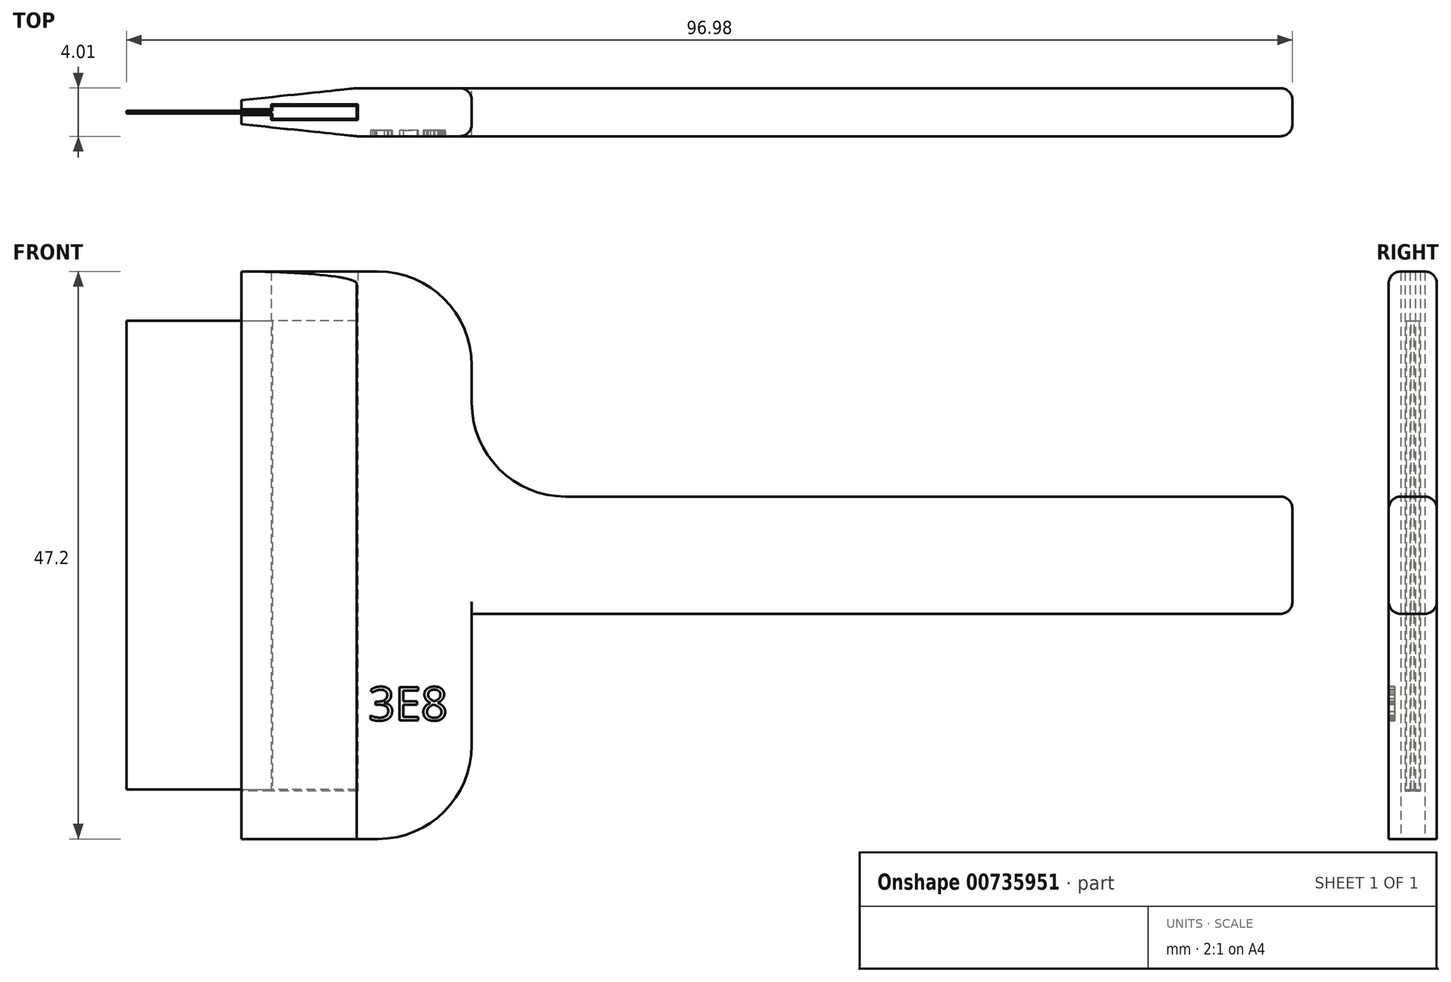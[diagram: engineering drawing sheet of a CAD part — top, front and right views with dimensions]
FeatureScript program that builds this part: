
annotation { "Feature Type Name" : "Feature", "Feature Type Description" : "" }
export const myFeature = defineFeature(function(context is Context, id is Id, definition is map)
    precondition{}
    {
        {
            assignVariable(context, id + "F0", {"name" : "res", "anyValue" : .1});
        }
        {
            assignVariable(context, id + "F1", {"name" : "razorthick", "anyValue" : .25});
        }
        {
            assignVariable(context, id + "F2", {"name" : "razorwidth", "anyValue" : 39});
        }
        {
            assignVariable(context, id + "F3", {"name" : "headthick", "anyValue" : 4});
        }
        {
            var Q0;
            Q0=qCreatedBy(makeId("Front.planeOp"),FACE);
            var sketch = newSketch(context, id + "F4", { "sketchPlane" : qUnion([Q0])});
            skLineSegment(sketch, "E0.bottom", {"start": v(-15.58, 0) * mm, "end": v(3.57, 0) * mm});
            skLineSegment(sketch, "E0.top", {"start": v(-15.58, 39) * mm, "end": v(3.57, 39) * mm});
            skLineSegment(sketch, "E0.left", {"start": v(-15.58, 0) * mm, "end": v(-15.58, 39) * mm});
            skLineSegment(sketch, "E0.right", {"start": v(3.57, 0) * mm, "end": v(3.57, 39) * mm});
            skSolve(sketch);
        }
        {
            var Q0;
            Q0=makeQuery(id+"F4.imprint","IMPRINT",FACE,{"disambiguationData":[TD([[makeQuery(id+"F4.imprint","IMPRINT",EDGE,{"derivedFrom":sQuery(id+"F4.wireOp",EDGE,"E0.bottom")}),1.0]])]});
            extrude(context, id + "F5", {"entities" : qUnion([Q0]), "depth" : (getVariable(context, 'razorthick')) * mm, "offsetDistance" : 25 * mm});
        }
        {
            var Q0;
            Q0=makeQuery(id+"F5.opExtrude","SWEPT_FACE",FACE,{"disambiguationData":[OSD([sQuery(id+"F4.wireOp",EDGE,"E0.bottom")])]});
            var sketch = newSketch(context, id + "F6", { "sketchPlane" : qUnion([Q0])});
            skLineSegment(sketch, "E1.bottom", {"start": v(3.57, 0.67) * mm, "end": v(-3.43, 0.67) * mm});
            skLineSegment(sketch, "E1.top", {"start": v(3.57, -0.41) * mm, "end": v(-3.43, -0.41) * mm});
            skLineSegment(sketch, "E1.left", {"start": v(3.57, 0.66) * mm, "end": v(3.57, -0.41) * mm});
            skLineSegment(sketch, "E1.right", {"start": v(-3.43, 0.66) * mm, "end": v(-3.43, -0.41) * mm});
            skPoint(sketch, "E2", {"position": v(3.57, 0.12) * mm});
            skSolve(sketch);
        }
        {
            var Q0;
            Q0 = qSketchRegion(id + "F6", true);
            var Q1;
            Q1=makeQuery(id+"F5.opExtrude","SWEPT_FACE",FACE,{"disambiguationData":[OSD([sQuery(id+"F4.wireOp",EDGE,"E0.top")])]});
            extrude(context, id + "F7", {"entities" : qUnion([Q0]), "operationType" : NewBodyOperationType.ADD, "endBound" : BoundingType.UP_TO_SURFACE, "oppositeDirection" : true, "depth" : 25 * mm, "endBoundEntityFace" : qUnion([Q1]), "offsetDistance" : 25 * mm});
        }
        {
            var Q0;
            Q0=makeQuery(id+"F7.boolean.opBoolean","MERGE",FACE,{"derivedFrom":[makeQuery(id+"F5.opExtrude","SWEPT_FACE",FACE,{"disambiguationData":[OSD([sQuery(id+"F4.wireOp",EDGE,"E0.bottom")])]}),makeQuery(id+"F7.opExtrude","CAP_FACE",FACE,{"disambiguationData":[OSD([sQuery(id+"F6.wireOp",EDGE,"E1.bottom"),sQuery(id+"F6.wireOp",EDGE,"E1.top"),sQuery(id+"F6.wireOp",EDGE,"E1.left"),sQuery(id+"F6.wireOp",EDGE,"E1.right")])],"isStart":true})]});
            cPlane(context, id + "F8", {"entities" : qUnion([Q0]), "cplaneType" : CPlaneType.OFFSET, "offset" : (getVariable(context, 'res')) * mm, "width" : 150 * mm, "height" : 150 * mm});
        }
        {
            var Q0;
            Q0=qCreatedBy(id+"F8.planeOp",FACE);
            var sketch = newSketch(context, id + "F9", { "sketchPlane" : qUnion([Q0])});
            skLineSegment(sketch, "E3.0.0", {"start": v(3.57, -0.41) * mm, "end": v(3.57, 0.67) * mm, "construction": true});
            skLineSegment(sketch, "E3.0.1", {"start": v(3.57, 0.67) * mm, "end": v(-3.43, 0.67) * mm, "construction": true});
            skLineSegment(sketch, "E3.0.2", {"start": v(-3.43, 0.67) * mm, "end": v(-3.43, 0.25) * mm, "construction": true});
            skLineSegment(sketch, "E3.0.3", {"start": v(-3.43, 0.25) * mm, "end": v(-15.58, 0.25) * mm, "construction": true});
            skLineSegment(sketch, "E3.0.4", {"start": v(-15.58, 0.25) * mm, "end": v(-15.58, 0) * mm, "construction": true});
            skLineSegment(sketch, "E3.0.5", {"start": v(-15.58, 0) * mm, "end": v(-3.43, 0) * mm, "construction": true});
            skLineSegment(sketch, "E3.0.6", {"start": v(-3.43, 0) * mm, "end": v(-3.43, -0.41) * mm, "construction": true});
            skLineSegment(sketch, "E3.0.7", {"start": v(-3.43, -0.41) * mm, "end": v(3.57, -0.41) * mm, "construction": true});
            skLineSegment(sketch, "E4.0", {"start": v(-3.53, -0.51) * mm, "end": v(3.67, -0.51) * mm});
            skLineSegment(sketch, "E4.1", {"start": v(-3.53, -0.1) * mm, "end": v(-3.53, -0.51) * mm});
            skLineSegment(sketch, "E4.2", {"start": v(3.67, -0.51) * mm, "end": v(3.67, 0.76) * mm});
            skLineSegment(sketch, "E4.3", {"start": v(-15.68, -0.1) * mm, "end": v(-3.53, -0.1) * mm});
            skLineSegment(sketch, "E4.4", {"start": v(3.67, 0.76) * mm, "end": v(-3.53, 0.76) * mm});
            skLineSegment(sketch, "E4.5", {"start": v(-3.53, 0.76) * mm, "end": v(-3.53, 0.35) * mm});
            skLineSegment(sketch, "E4.6", {"start": v(-3.53, 0.35) * mm, "end": v(-15.68, 0.35) * mm});
            skLineSegment(sketch, "E4.7", {"start": v(-15.68, 0.35) * mm, "end": v(-15.68, -0.1) * mm});
            skLineSegment(sketch, "E5", {"start": v(3.57, 0.12) * mm, "end": v(-6, 0.12) * mm, "construction": true});
            skLineSegment(sketch, "E6.bottom", {"start": v(-6, -1.88) * mm, "end": v(13.15, -1.88) * mm});
            skLineSegment(sketch, "E6.top", {"start": v(-6, 2.12) * mm, "end": v(13.15, 2.12) * mm});
            skLineSegment(sketch, "E6.left", {"start": v(-6, -1.88) * mm, "end": v(-6, 2.12) * mm});
            skLineSegment(sketch, "E6.right", {"start": v(13.15, -1.88) * mm, "end": v(13.15, 2.12) * mm});
            skPoint(sketch, "E6.middle", {"position": v(3.57, 0.12) * mm});
            skLineSegment(sketch, "E7", {"start": v(-6, 1.12) * mm, "end": v(3.57, 2.12) * mm});
            skLineSegment(sketch, "E8.MirrorCS", {"start": v(-6, -0.87) * mm, "end": v(3.57, -1.87) * mm});
            skSolve(sketch);
        }
        {
            var Q0;
            Q0=makeQuery(id+"F9.imprint","IMPRINT",FACE,{"disambiguationData":[TD([[makeQuery(id+"F9.imprint","IMPRINT",EDGE,{"derivedFrom":sQuery(id+"F9.wireOp",EDGE,"E4.0")}),-1.0]])]});
            extrude(context, id + "F10", {"entities" : qUnion([Q0]), "oppositeDirection" : true, "depth" : (getVariable(context, 'razorwidth') + (2 * getVariable(context, 'res')) + getVariable(context, 'headthick')) * mm, "offsetDistance" : 25 * mm});
        }
        {
            var Q0;
            Q0=makeQuery(id+"F10.opExtrude","CAP_FACE",FACE,{"disambiguationData":[OSD([sQuery(id+"F9.wireOp",EDGE,"E4.0"),sQuery(id+"F9.wireOp",EDGE,"E4.1"),sQuery(id+"F9.wireOp",EDGE,"E4.2"),sQuery(id+"F9.wireOp",EDGE,"E4.3"),sQuery(id+"F9.wireOp",EDGE,"E4.4"),sQuery(id+"F9.wireOp",EDGE,"E4.5"),sQuery(id+"F9.wireOp",EDGE,"E4.6"),sQuery(id+"F9.wireOp",EDGE,"E6.bottom"),sQuery(id+"F9.wireOp",EDGE,"E6.top"),sQuery(id+"F9.wireOp",EDGE,"E6.left"),sQuery(id+"F9.wireOp",EDGE,"E6.right"),sQuery(id+"F9.wireOp",EDGE,"E7"),sQuery(id+"F9.wireOp",EDGE,"E8.MirrorCS")])],"isStart":true});
            var sketch = newSketch(context, id + "F11", { "sketchPlane" : qUnion([Q0])});
            skLineSegment(sketch, "E9.0.0", {"start": v(-6, -0.1) * mm, "end": v(-6, -0.87) * mm});
            skLineSegment(sketch, "E9.0.1", {"start": v(-6, -0.87) * mm, "end": v(3.57, -1.88) * mm});
            skLineSegment(sketch, "E9.0.2", {"start": v(3.57, -1.88) * mm, "end": v(13.15, -1.88) * mm});
            skLineSegment(sketch, "E9.0.3", {"start": v(13.15, -1.88) * mm, "end": v(13.15, 2.12) * mm});
            skLineSegment(sketch, "E9.0.4", {"start": v(13.15, 2.12) * mm, "end": v(3.57, 2.12) * mm});
            skLineSegment(sketch, "E9.0.5", {"start": v(3.57, 2.12) * mm, "end": v(-6, 1.12) * mm});
            skLineSegment(sketch, "E9.0.6", {"start": v(-6, 1.12) * mm, "end": v(-6, 0.35) * mm});
            skLineSegment(sketch, "E9.0.7", {"start": v(-6, 0.35) * mm, "end": v(-3.53, 0.35) * mm, "construction": true});
            skLineSegment(sketch, "E9.0.8", {"start": v(-3.53, 0.35) * mm, "end": v(-3.53, 0.76) * mm, "construction": true});
            skLineSegment(sketch, "E9.0.9", {"start": v(-3.53, 0.76) * mm, "end": v(3.67, 0.76) * mm, "construction": true});
            skLineSegment(sketch, "E9.0.10", {"start": v(3.67, 0.76) * mm, "end": v(3.67, -0.51) * mm, "construction": true});
            skLineSegment(sketch, "E9.0.11", {"start": v(3.67, -0.51) * mm, "end": v(-3.53, -0.51) * mm, "construction": true});
            skLineSegment(sketch, "E9.0.12", {"start": v(-3.53, -0.51) * mm, "end": v(-3.53, -0.1) * mm, "construction": true});
            skLineSegment(sketch, "E9.0.13", {"start": v(-3.53, -0.1) * mm, "end": v(-6, -0.1) * mm, "construction": true});
            skLineSegment(sketch, "E10", {"start": v(-6, -0.1) * mm, "end": v(-6, 0.35) * mm});
            skSolve(sketch);
        }
        {
            var Q0;
            Q0 = qSketchRegion(id + "F11", true);
            extrude(context, id + "F12", {"entities" : qUnion([Q0]), "operationType" : NewBodyOperationType.ADD, "depth" : (getVariable(context, 'headthick')) * mm, "offsetDistance" : 25 * mm});
        }
        {
            var Q0;
            Q0=makeQuery(id+"F12.boolean.opBoolean","MERGE",FACE,{"derivedFrom":[makeQuery(id+"F10.opExtrude","SWEPT_FACE",FACE,{"disambiguationData":[OSD([sQuery(id+"F9.wireOp",EDGE,"E6.right")])]}),makeQuery(id+"F12.opExtrude","SWEPT_FACE",FACE,{"disambiguationData":[OSD([sQuery(id+"F11.wireOp",EDGE,"E9.0.3")])]})]});
            var sketch = newSketch(context, id + "F13", { "sketchPlane" : qUnion([Q0])});
            skLineSegment(sketch, "E11", {"start": v(-2.13, -4.1) * mm, "end": v(1.88, 43.1) * mm, "construction": true});
            skPoint(sketch, "E12", {"position": v(-0.12, 19.5) * mm});
            skLineSegment(sketch, "E13.bottom", {"start": v(-2.12, 24.37) * mm, "end": v(1.88, 24.37) * mm});
            skLineSegment(sketch, "E13.top", {"start": v(-2.12, 14.62) * mm, "end": v(1.88, 14.62) * mm});
            skLineSegment(sketch, "E13.left", {"start": v(-2.12, 24.37) * mm, "end": v(-2.12, 14.62) * mm});
            skLineSegment(sketch, "E13.right", {"start": v(1.87, 24.37) * mm, "end": v(1.87, 14.62) * mm});
            skSolve(sketch);
        }
        {
            var Q0;
            Q0 = qSketchRegion(id + "F13", true);
            extrude(context, id + "F14", {"entities" : qUnion([Q0]), "operationType" : NewBodyOperationType.ADD, "depth" : (1.75 * getVariable(context, 'razorwidth')) * mm, "offsetDistance" : 25 * mm});
        }
        {
            var Q0;
            Q0=makeQuery(id+"F14.opExtrude","CAP_EDGE",EDGE,{"disambiguationData":[OSD([sQuery(id+"F13.wireOp",EDGE,"E13.bottom")])],"isStart":true});
            var Q1;
            Q1=makeQuery(id+"F10.opExtrude","CAP_EDGE",EDGE,{"disambiguationData":[OSD([sQuery(id+"F9.wireOp",EDGE,"E6.right")])],"isStart":false});
            var Q2;
            Q2=makeQuery(id+"F12.opExtrude","CAP_EDGE",EDGE,{"disambiguationData":[OSD([sQuery(id+"F11.wireOp",EDGE,"E9.0.3")])],"isStart":false});
            var Q3;
            Q3=makeQuery(id+"F14.opExtrude","CAP_EDGE",EDGE,{"disambiguationData":[OSD([sQuery(id+"F13.wireOp",EDGE,"E13.top")])],"isStart":true});
            fillet(context, id + "F15", {"entities" : qUnion([Q0, Q1, Q2, Q3]), "radius" : (.2 * getVariable(context, 'razorwidth')) * mm, "tangentPropagation" : true, "allowEdgeOverflow" : false});
        }
        {
            var Q0;
            Q0=makeQuery(id+"F14.opExtrude","CAP_FACE",FACE,{"disambiguationData":[OSD([sQuery(id+"F13.wireOp",EDGE,"E13.bottom"),sQuery(id+"F13.wireOp",EDGE,"E13.top"),sQuery(id+"F13.wireOp",EDGE,"E13.left"),sQuery(id+"F13.wireOp",EDGE,"E13.right")])],"isStart":false});
            var Q1;
            Q1=makeQuery(id+"F14.opExtrude","SWEPT_EDGE",EDGE,{"disambiguationData":[OSD([sQuery(id+"F9.wireOp",EDGE,"E6.top"),sQuery(id+"F9.wireOp",EDGE,"E6.right"),sQuery(id+"F11.wireOp",EDGE,"E9.0.3"),sQuery(id+"F11.wireOp",EDGE,"E9.0.4"),sQuery(id+"F13.wireOp",EDGE,"E13.bottom"),sQuery(id+"F13.wireOp",EDGE,"E13.left")])]});
            var Q2;
            Q2=makeQuery(id+"F14.opExtrude","SWEPT_EDGE",EDGE,{"disambiguationData":[OSD([sQuery(id+"F9.wireOp",EDGE,"E6.bottom"),sQuery(id+"F9.wireOp",EDGE,"E6.right"),sQuery(id+"F11.wireOp",EDGE,"E9.0.2"),sQuery(id+"F11.wireOp",EDGE,"E9.0.3"),sQuery(id+"F13.wireOp",EDGE,"E13.bottom"),sQuery(id+"F13.wireOp",EDGE,"E13.right")])]});
            var Q3;
            Q3=makeQuery(id+"F14.opExtrude","SWEPT_EDGE",EDGE,{"disambiguationData":[OSD([sQuery(id+"F9.wireOp",EDGE,"E6.top"),sQuery(id+"F9.wireOp",EDGE,"E6.right"),sQuery(id+"F11.wireOp",EDGE,"E9.0.3"),sQuery(id+"F11.wireOp",EDGE,"E9.0.4"),sQuery(id+"F13.wireOp",EDGE,"E13.top"),sQuery(id+"F13.wireOp",EDGE,"E13.left")])]});
            var Q4;
            Q4=makeQuery(id+"F14.opExtrude","SWEPT_EDGE",EDGE,{"disambiguationData":[OSD([sQuery(id+"F9.wireOp",EDGE,"E6.bottom"),sQuery(id+"F9.wireOp",EDGE,"E6.right"),sQuery(id+"F11.wireOp",EDGE,"E9.0.2"),sQuery(id+"F11.wireOp",EDGE,"E9.0.3"),sQuery(id+"F13.wireOp",EDGE,"E13.top"),sQuery(id+"F13.wireOp",EDGE,"E13.right")])]});
            fillet(context, id + "F16", {"entities" : qUnion([Q0, Q1, Q2, Q3, Q4]), "radius" : 1 * mm, "tangentPropagation" : true, "allowEdgeOverflow" : false});
        }
        {
            var Q0;
            Q0=makeQuery(id+"F14.boolean.opBoolean","MERGE",FACE,{"derivedFrom":[makeQuery(id+"F12.boolean.opBoolean","MERGE",FACE,{"derivedFrom":[makeQuery(id+"F10.opExtrude","SWEPT_FACE",FACE,{"disambiguationData":[OSD([sQuery(id+"F9.wireOp",EDGE,"E6.top")])]}),makeQuery(id+"F12.opExtrude","SWEPT_FACE",FACE,{"disambiguationData":[OSD([sQuery(id+"F11.wireOp",EDGE,"E9.0.4")])]})]}),makeQuery(id+"F14.opExtrude","SWEPT_FACE",FACE,{"disambiguationData":[OSD([sQuery(id+"F13.wireOp",EDGE,"E13.left")])]})]});
            var sketch = newSketch(context, id + "F17", { "sketchPlane" : qUnion([Q0])});
            skLineSegment(sketch, "E14", {"start": v(20.95, 15.62) * mm, "end": v(3.57, 15.62) * mm, "construction": true});
            skLineSegment(sketch, "E15", {"start": v(3.57, 15.62) * mm, "end": v(10.16, -1.1) * mm, "construction": true});
            skLineSegment(sketch, "E16", {"start": v(6.86, 7.26) * mm, "end": v(7.86, 7.26) * mm, "construction": true});
            skText(sketch, "E17", { "text": "3E8", "fontName": "OpenSans-Regular.ttf"});
            const initialGuessF17  = {"E17": [0.00453, 0.00576, 1, 0, 0.0028]};
            skSetInitialGuess(sketch, initialGuessF17);
            skSolve(sketch);
        }
        {
            var Q0;
            Q0 = qSketchRegion(id + "F17", true);
            extrude(context, id + "F18", {"entities" : qUnion([Q0]), "operationType" : NewBodyOperationType.REMOVE, "oppositeDirection" : true, "depth" : .5 * mm, "offsetDistance" : 25 * mm});
        }
    });
